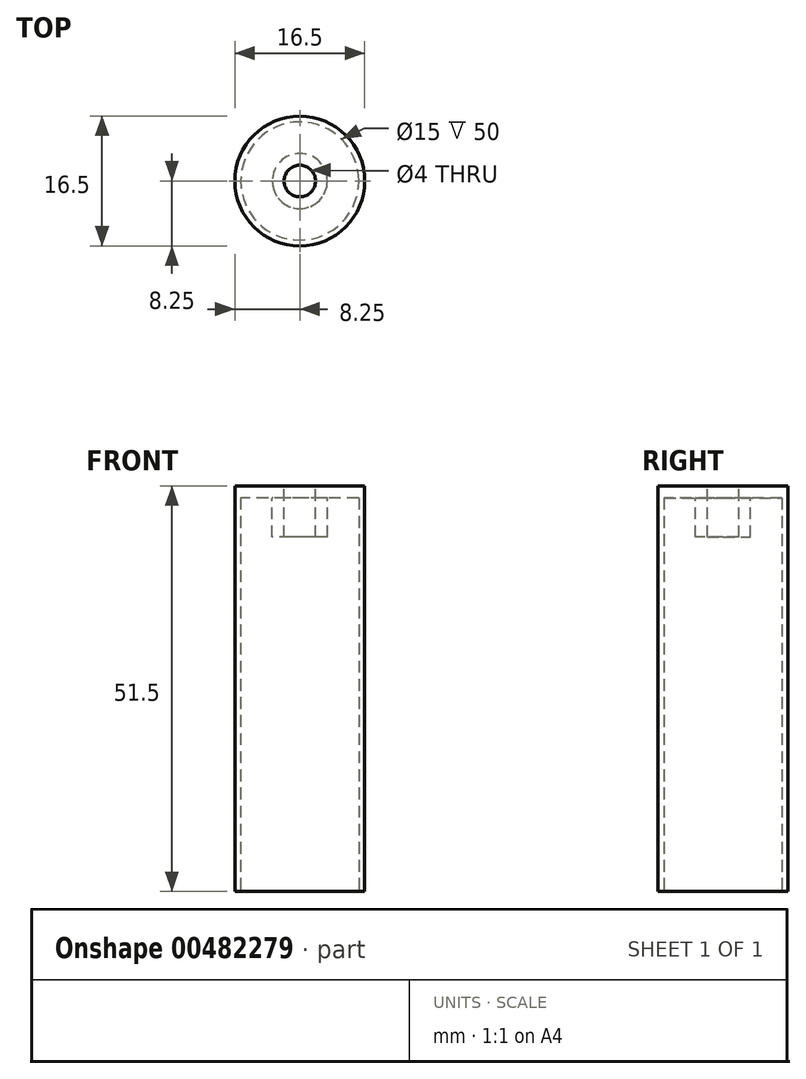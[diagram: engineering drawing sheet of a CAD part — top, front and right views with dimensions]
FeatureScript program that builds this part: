
annotation { "Feature Type Name" : "Feature", "Feature Type Description" : "" }
export const myFeature = defineFeature(function(context is Context, id is Id, definition is map)
    precondition{}
    {
        {
            var Q0;
            Q0=qCreatedBy(makeId("Top.planeOp"),FACE);
            var sketch = newSketch(context, id + "F0", { "sketchPlane" : qUnion([Q0])});
            skCircle(sketch, "E0", {"center": v(0, 0) * mm, "radius": 7.5 * mm});
            skCircle(sketch, "E1", {"center": v(0, 0) * mm, "radius": 8.25 * mm});
            skSolve(sketch);
        }
        {
            var Q0;
            Q0 = qSketchRegion(id + "F0", true);
            extrude(context, id + "F1", {"entities" : qUnion([Q0]), "depth" : 50 * mm});
        }
        {
            var Q0;
            Q0=makeQuery(id+"F1.opExtrude","CAP_FACE",FACE,{"disambiguationData":[OSD([sQuery(id+"F0.wireOp",EDGE,"E0"),sQuery(id+"F0.wireOp",EDGE,"E1")])],"isStart":false});
            var sketch = newSketch(context, id + "F2", { "sketchPlane" : qUnion([Q0])});
            skCircle(sketch, "E2.0", {"center": v(0, 0) * mm, "radius": 8.25 * mm});
            skSolve(sketch);
        }
        {
            var Q0;
            Q0 = qSketchRegion(id + "F2", true);
            extrude(context, id + "F3", {"entities" : qUnion([Q0]), "operationType" : NewBodyOperationType.ADD, "depth" : 1.5 * mm});
        }
        {
            var Q0;
            Q0=makeQuery(id+"F3.opExtrude","CAP_FACE",FACE,{"disambiguationData":[OSD([sQuery(id+"F2.wireOp",EDGE,"E2.0")])],"isStart":false});
            var sketch = newSketch(context, id + "F4", { "sketchPlane" : qUnion([Q0])});
            skCircle(sketch, "E3", {"center": v(0, 0) * mm, "radius": 2 * mm});
            skSolve(sketch);
        }
        {
            var Q0;
            Q0 = qSketchRegion(id + "F4", true);
            extrude(context, id + "F5", {"entities" : qUnion([Q0]), "operationType" : NewBodyOperationType.REMOVE, "oppositeDirection" : true, "depth" : 25 * mm});
        }
        {
            var Q0;
            Q0=makeQuery(id+"F3.opExtrude","CAP_FACE",FACE,{"disambiguationData":[OSD([sQuery(id+"F2.wireOp",EDGE,"E2.0")])],"isStart":true});
            var sketch = newSketch(context, id + "F6", { "sketchPlane" : qUnion([Q0])});
            skCircle(sketch, "E4.0", {"center": v(0, 0) * mm, "radius": 2 * mm});
            skCircle(sketch, "E5", {"center": v(0, 0) * mm, "radius": 3.5 * mm});
            skSolve(sketch);
        }
        {
            var Q0;
            Q0 = qSketchRegion(id + "F6", true);
            extrude(context, id + "F7", {"entities" : qUnion([Q0]), "operationType" : NewBodyOperationType.ADD, "depth" : 5 * mm});
        }
    });
